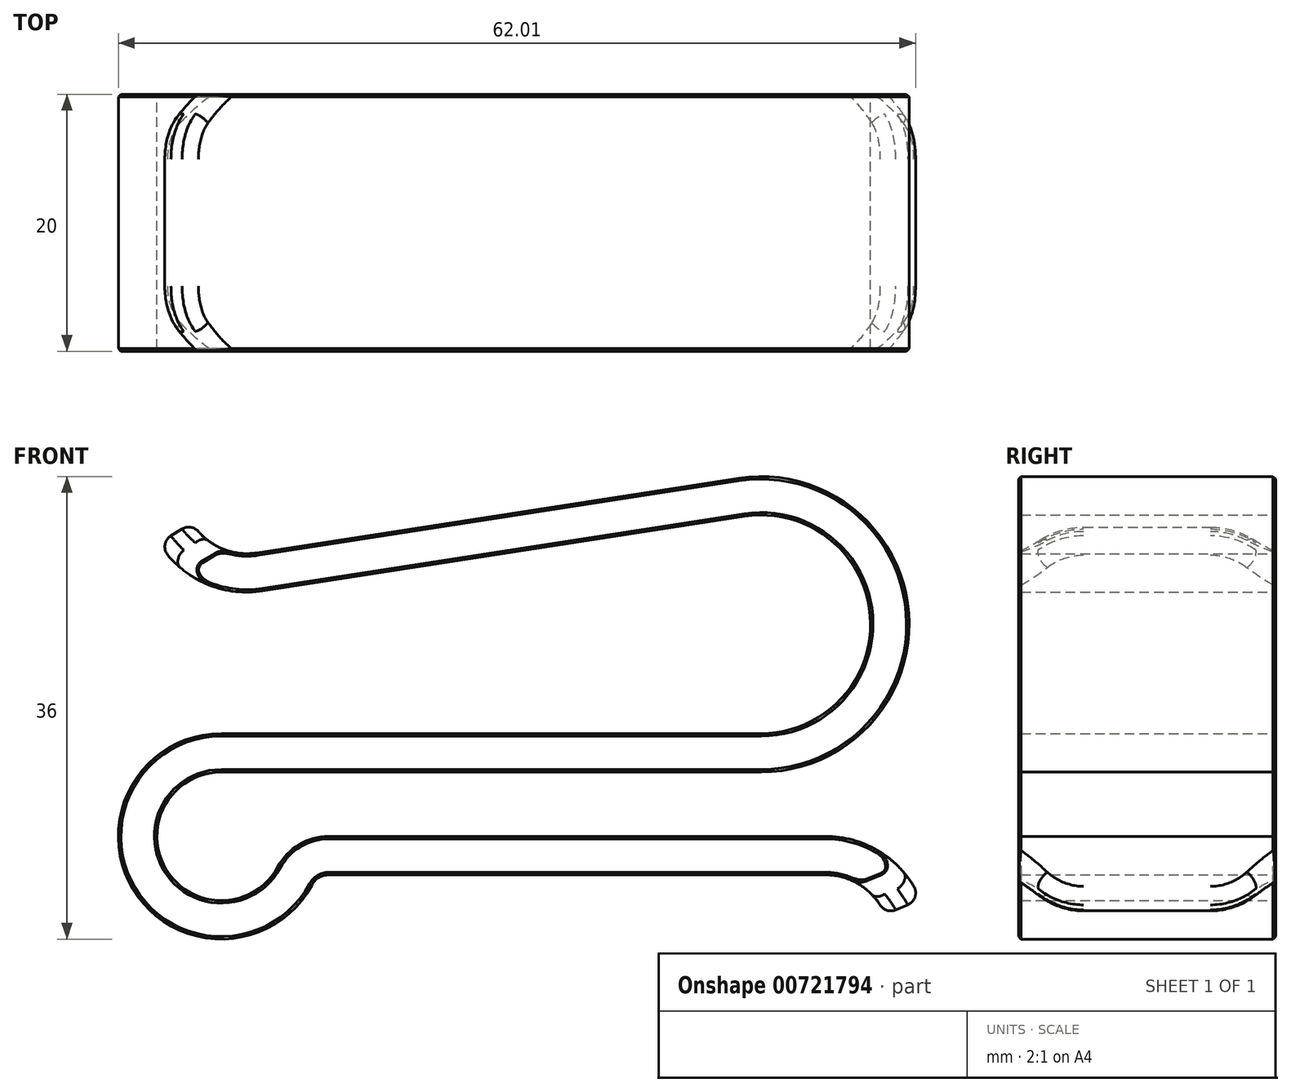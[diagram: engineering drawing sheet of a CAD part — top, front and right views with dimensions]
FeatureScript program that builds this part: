
annotation { "Feature Type Name" : "Feature", "Feature Type Description" : "" }
export const myFeature = defineFeature(function(context is Context, id is Id, definition is map)
    precondition{}
    {
        {
            var Q0;
            Q0=qCreatedBy(makeId("Front.planeOp"),FACE);
            var sketch = newSketch(context, id + "F0", { "sketchPlane" : qUnion([Q0])});
            skLineSegment(sketch, "E0", {"start": v(-42, 0) * mm, "end": v(0, 0) * mm, "construction": true});
            skArc(sketch, "E1", {"start": v(0, 0) * mm, "mid": v(9.97, 10.77) * mm, "end": v(-1.53, 19.88) * mm, "construction": true});
            skLineSegment(sketch, "E2", {"start": v(-1.53, 19.88) * mm, "end": v(-39, 14.08) * mm, "construction": true});
            skArc(sketch, "E3", {"start": v(-45.55, 17.11) * mm, "mid": v(-42.74, 14.6) * mm, "end": v(-39, 14.08) * mm, "construction": true});
            skArc(sketch, "E4", {"start": v(-42, 0) * mm, "mid": v(-47.58, -9.83) * mm, "end": v(-36.28, -9.58) * mm, "construction": true});
            skArc(sketch, "E5", {"start": v(-33.63, -8) * mm, "mid": v(-35.17, -8.42) * mm, "end": v(-36.28, -9.58) * mm, "construction": true});
            skLineSegment(sketch, "E6", {"start": v(-33.63, -8) * mm, "end": v(5, -8) * mm, "construction": true});
            skArc(sketch, "E7", {"start": v(11, -12) * mm, "mid": v(8.6, -9.1) * mm, "end": v(5, -8) * mm, "construction": true});
            skArc(sketch, "E8.0", {"start": v(-44.27, 17.9) * mm, "mid": v(-42.1, 15.96) * mm, "end": v(-39.23, 15.56) * mm});
            skLineSegment(sketch, "E8.1", {"start": v(-1.76, 21.36) * mm, "end": v(-39.23, 15.56) * mm});
            skArc(sketch, "E8.2", {"start": v(0, -1.5) * mm, "mid": v(11.47, 10.88) * mm, "end": v(-1.76, 21.36) * mm});
            skLineSegment(sketch, "E8.3", {"start": v(-42, -1.5) * mm, "end": v(0, -1.5) * mm});
            skArc(sketch, "E8.4", {"start": v(12.38, -11.42) * mm, "mid": v(9.44, -7.84) * mm, "end": v(5, -6.5) * mm});
            skLineSegment(sketch, "E8.5", {"start": v(-33.63, -6.5) * mm, "end": v(5, -6.5) * mm});
            skArc(sketch, "E8.6", {"start": v(-33.63, -6.5) * mm, "mid": v(-35.94, -7.14) * mm, "end": v(-37.6, -8.87) * mm});
            skArc(sketch, "E8.7", {"start": v(-42, -1.5) * mm, "mid": v(-46.3, -9.06) * mm, "end": v(-37.6, -8.87) * mm});
            skArc(sketch, "E9.0", {"start": v(9.62, -12.58) * mm, "mid": v(7.77, -10.34) * mm, "end": v(5, -9.5) * mm});
            skLineSegment(sketch, "E9.1", {"start": v(-33.63, -9.5) * mm, "end": v(5, -9.5) * mm});
            skArc(sketch, "E9.2", {"start": v(-33.63, -9.5) * mm, "mid": v(-34.4, -9.71) * mm, "end": v(-34.95, -10.29) * mm});
            skArc(sketch, "E9.3", {"start": v(-42, 1.5) * mm, "mid": v(-48.87, -10.6) * mm, "end": v(-34.95, -10.29) * mm});
            skArc(sketch, "E9.4", {"start": v(-46.83, 16.33) * mm, "mid": v(-43.37, 13.24) * mm, "end": v(-38.78, 12.6) * mm});
            skLineSegment(sketch, "E9.5", {"start": v(-1.3, 18.4) * mm, "end": v(-38.78, 12.6) * mm});
            skArc(sketch, "E9.6", {"start": v(0, 1.5) * mm, "mid": v(8.47, 10.65) * mm, "end": v(-1.3, 18.4) * mm});
            skLineSegment(sketch, "E9.7", {"start": v(-42, 1.5) * mm, "end": v(0, 1.5) * mm});
            skLineSegment(sketch, "E10", {"start": v(12.38, -11.42) * mm, "end": v(9.62, -12.58) * mm});
            skLineSegment(sketch, "E11", {"start": v(-44.27, 17.9) * mm, "end": v(-46.83, 16.33) * mm});
            skSolve(sketch);
        }
        {
            var Q0;
            Q0=makeQuery(id+"F0.imprint","IMPRINT",FACE,{"disambiguationData":[TD([[makeQuery(id+"F0.imprint","IMPRINT",EDGE,{"derivedFrom":sQuery(id+"F0.wireOp",EDGE,"E8.0")}),-1.0]])]});
            extrude(context, id + "F1", {"entities" : qUnion([Q0]), "depth" : 20 * mm, "offsetDistance" : 25 * mm});
        }
        {
            var Q0;
            Q0=makeQuery(id+"F1.opExtrude","CAP_EDGE",EDGE,{"disambiguationData":[OSD([sQuery(id+"F0.wireOp",EDGE,"E10")])],"isStart":false});
            var Q1;
            Q1=makeQuery(id+"F1.opExtrude","CAP_EDGE",EDGE,{"disambiguationData":[OSD([sQuery(id+"F0.wireOp",EDGE,"E10")])],"isStart":true});
            var Q2;
            Q2=makeQuery(id+"F1.opExtrude","CAP_EDGE",EDGE,{"disambiguationData":[OSD([sQuery(id+"F0.wireOp",EDGE,"E11")])],"isStart":false});
            var Q3;
            Q3=makeQuery(id+"F1.opExtrude","CAP_EDGE",EDGE,{"disambiguationData":[OSD([sQuery(id+"F0.wireOp",EDGE,"E11")])],"isStart":true});
            chamfer(context, id + "F2", {"entities" : qUnion([Q0, Q1, Q2, Q3]), "width" : 3 * mm, "tangentPropagation" : true});
        }
        {
            var Q0;
            {var subQ0=sQuery(id+"F0.wireOp",EDGE,"E11");Q0=makeQuery(id+"F2.opChamfer","BLEND_EDGE",EDGE,{"blendedFrom":[makeQuery(id+"F1.opExtrude","CAP_EDGE",EDGE,{"disambiguationData":[OSD([subQ0])],"isStart":false}),makeQuery(id+"F1.opExtrude","SWEPT_FACE",FACE,{"disambiguationData":[OSD([subQ0])]})],"blendedInto":[makeQuery(id+"F1.opExtrude","SWEPT_FACE",FACE,{"disambiguationData":[OSD([subQ0])]})]});}
            var Q1;
            {var subQ0=sQuery(id+"F0.wireOp",EDGE,"E11");Q1=makeQuery(id+"F2.opChamfer","BLEND_EDGE",EDGE,{"blendedFrom":[makeQuery(id+"F1.opExtrude","CAP_EDGE",EDGE,{"disambiguationData":[OSD([subQ0])],"isStart":true}),makeQuery(id+"F1.opExtrude","SWEPT_FACE",FACE,{"disambiguationData":[OSD([subQ0])]})],"blendedInto":[makeQuery(id+"F1.opExtrude","SWEPT_FACE",FACE,{"disambiguationData":[OSD([subQ0])]})]});}
            var Q2;
            {var subQ0=sQuery(id+"F0.wireOp",EDGE,"E10");Q2=makeQuery(id+"F2.opChamfer","BLEND_EDGE",EDGE,{"blendedFrom":[makeQuery(id+"F1.opExtrude","CAP_EDGE",EDGE,{"disambiguationData":[OSD([subQ0])],"isStart":true}),makeQuery(id+"F1.opExtrude","SWEPT_FACE",FACE,{"disambiguationData":[OSD([subQ0])]})],"blendedInto":[makeQuery(id+"F1.opExtrude","SWEPT_FACE",FACE,{"disambiguationData":[OSD([subQ0])]})]});}
            var Q3;
            {var subQ0=sQuery(id+"F0.wireOp",EDGE,"E10");Q3=makeQuery(id+"F2.opChamfer","BLEND_EDGE",EDGE,{"blendedFrom":[makeQuery(id+"F1.opExtrude","CAP_EDGE",EDGE,{"disambiguationData":[OSD([subQ0])],"isStart":false}),makeQuery(id+"F1.opExtrude","SWEPT_FACE",FACE,{"disambiguationData":[OSD([subQ0])]})],"blendedInto":[makeQuery(id+"F1.opExtrude","SWEPT_FACE",FACE,{"disambiguationData":[OSD([subQ0])]})]});}
            fillet(context, id + "F3", {"entities" : qUnion([Q0, Q1, Q2, Q3]), "radius" : 5 * mm, "tangentPropagation" : true, "allowEdgeOverflow" : false});
        }
        {
            var Q0;
            Q0=makeQuery(id+"F2.opChamfer","BLEND_EDGE",EDGE,{"blendedFrom":[makeQuery(id+"F1.opExtrude","CAP_EDGE",EDGE,{"disambiguationData":[OSD([sQuery(id+"F0.wireOp",EDGE,"E10")])],"isStart":true}),makeQuery(id+"F1.opExtrude","SWEPT_FACE",FACE,{"disambiguationData":[OSD([sQuery(id+"F0.wireOp",EDGE,"E9.0")])]})],"blendedInto":[makeQuery(id+"F1.opExtrude","SWEPT_FACE",FACE,{"disambiguationData":[OSD([sQuery(id+"F0.wireOp",EDGE,"E9.0")])]})]});
            var Q1;
            {var subQ0=sQuery(id+"F0.wireOp",EDGE,"E10");Q1=makeQuery(id+"F3.opFillet","BLEND_EDGE",EDGE,{"blendedFrom":[makeQuery(id+"F2.opChamfer","BLEND_EDGE",EDGE,{"blendedFrom":[makeQuery(id+"F1.opExtrude","CAP_EDGE",EDGE,{"disambiguationData":[OSD([subQ0])],"isStart":true}),makeQuery(id+"F1.opExtrude","SWEPT_FACE",FACE,{"disambiguationData":[OSD([subQ0])]})],"blendedInto":[makeQuery(id+"F1.opExtrude","SWEPT_FACE",FACE,{"disambiguationData":[OSD([subQ0])]})]}),makeQuery(id+"F1.opExtrude","SWEPT_FACE",FACE,{"disambiguationData":[OSD([sQuery(id+"F0.wireOp",EDGE,"E9.0")])]})],"blendedInto":[makeQuery(id+"F1.opExtrude","SWEPT_FACE",FACE,{"disambiguationData":[OSD([sQuery(id+"F0.wireOp",EDGE,"E9.0")])]})]});}
            var Q2;
            Q2=makeQuery(id+"F1.opExtrude","SWEPT_EDGE",EDGE,{"disambiguationData":[OSD([sQuery(id+"F0.wireOp",EDGE,"E9.0"),sQuery(id+"F0.wireOp",EDGE,"E10")])]});
            var Q3;
            {var subQ0=sQuery(id+"F0.wireOp",EDGE,"E10");Q3=makeQuery(id+"F3.opFillet","BLEND_EDGE",EDGE,{"blendedFrom":[makeQuery(id+"F2.opChamfer","BLEND_EDGE",EDGE,{"blendedFrom":[makeQuery(id+"F1.opExtrude","CAP_EDGE",EDGE,{"disambiguationData":[OSD([subQ0])],"isStart":false}),makeQuery(id+"F1.opExtrude","SWEPT_FACE",FACE,{"disambiguationData":[OSD([subQ0])]})],"blendedInto":[makeQuery(id+"F1.opExtrude","SWEPT_FACE",FACE,{"disambiguationData":[OSD([subQ0])]})]}),makeQuery(id+"F1.opExtrude","SWEPT_FACE",FACE,{"disambiguationData":[OSD([sQuery(id+"F0.wireOp",EDGE,"E9.0")])]})],"blendedInto":[makeQuery(id+"F1.opExtrude","SWEPT_FACE",FACE,{"disambiguationData":[OSD([sQuery(id+"F0.wireOp",EDGE,"E9.0")])]})]});}
            var Q4;
            Q4=makeQuery(id+"F2.opChamfer","BLEND_EDGE",EDGE,{"blendedFrom":[makeQuery(id+"F1.opExtrude","CAP_EDGE",EDGE,{"disambiguationData":[OSD([sQuery(id+"F0.wireOp",EDGE,"E10")])],"isStart":false}),makeQuery(id+"F1.opExtrude","SWEPT_FACE",FACE,{"disambiguationData":[OSD([sQuery(id+"F0.wireOp",EDGE,"E9.0")])]})],"blendedInto":[makeQuery(id+"F1.opExtrude","SWEPT_FACE",FACE,{"disambiguationData":[OSD([sQuery(id+"F0.wireOp",EDGE,"E9.0")])]})]});
            var Q5;
            Q5=makeQuery(id+"F1.opExtrude","SWEPT_EDGE",EDGE,{"disambiguationData":[OSD([sQuery(id+"F0.wireOp",EDGE,"E8.4"),sQuery(id+"F0.wireOp",EDGE,"E10")])]});
            var Q6;
            {var subQ0=sQuery(id+"F0.wireOp",EDGE,"E10");Q6=makeQuery(id+"F3.opFillet","BLEND_EDGE",EDGE,{"blendedFrom":[makeQuery(id+"F2.opChamfer","BLEND_EDGE",EDGE,{"blendedFrom":[makeQuery(id+"F1.opExtrude","CAP_EDGE",EDGE,{"disambiguationData":[OSD([subQ0])],"isStart":true}),makeQuery(id+"F1.opExtrude","SWEPT_FACE",FACE,{"disambiguationData":[OSD([subQ0])]})],"blendedInto":[makeQuery(id+"F1.opExtrude","SWEPT_FACE",FACE,{"disambiguationData":[OSD([subQ0])]})]}),makeQuery(id+"F1.opExtrude","SWEPT_FACE",FACE,{"disambiguationData":[OSD([sQuery(id+"F0.wireOp",EDGE,"E8.4")])]})],"blendedInto":[makeQuery(id+"F1.opExtrude","SWEPT_FACE",FACE,{"disambiguationData":[OSD([sQuery(id+"F0.wireOp",EDGE,"E8.4")])]})]});}
            var Q7;
            Q7=makeQuery(id+"F2.opChamfer","BLEND_EDGE",EDGE,{"blendedFrom":[makeQuery(id+"F1.opExtrude","CAP_EDGE",EDGE,{"disambiguationData":[OSD([sQuery(id+"F0.wireOp",EDGE,"E10")])],"isStart":true}),makeQuery(id+"F1.opExtrude","SWEPT_FACE",FACE,{"disambiguationData":[OSD([sQuery(id+"F0.wireOp",EDGE,"E8.4")])]})],"blendedInto":[makeQuery(id+"F1.opExtrude","SWEPT_FACE",FACE,{"disambiguationData":[OSD([sQuery(id+"F0.wireOp",EDGE,"E8.4")])]})]});
            var Q8;
            {var subQ0=sQuery(id+"F0.wireOp",EDGE,"E10");Q8=makeQuery(id+"F3.opFillet","BLEND_EDGE",EDGE,{"blendedFrom":[makeQuery(id+"F2.opChamfer","BLEND_EDGE",EDGE,{"blendedFrom":[makeQuery(id+"F1.opExtrude","CAP_EDGE",EDGE,{"disambiguationData":[OSD([subQ0])],"isStart":false}),makeQuery(id+"F1.opExtrude","SWEPT_FACE",FACE,{"disambiguationData":[OSD([subQ0])]})],"blendedInto":[makeQuery(id+"F1.opExtrude","SWEPT_FACE",FACE,{"disambiguationData":[OSD([subQ0])]})]}),makeQuery(id+"F1.opExtrude","SWEPT_FACE",FACE,{"disambiguationData":[OSD([sQuery(id+"F0.wireOp",EDGE,"E8.4")])]})],"blendedInto":[makeQuery(id+"F1.opExtrude","SWEPT_FACE",FACE,{"disambiguationData":[OSD([sQuery(id+"F0.wireOp",EDGE,"E8.4")])]})]});}
            var Q9;
            Q9=makeQuery(id+"F2.opChamfer","BLEND_EDGE",EDGE,{"blendedFrom":[makeQuery(id+"F1.opExtrude","CAP_EDGE",EDGE,{"disambiguationData":[OSD([sQuery(id+"F0.wireOp",EDGE,"E10")])],"isStart":false}),makeQuery(id+"F1.opExtrude","SWEPT_FACE",FACE,{"disambiguationData":[OSD([sQuery(id+"F0.wireOp",EDGE,"E8.4")])]})],"blendedInto":[makeQuery(id+"F1.opExtrude","SWEPT_FACE",FACE,{"disambiguationData":[OSD([sQuery(id+"F0.wireOp",EDGE,"E8.4")])]})]});
            var Q10;
            Q10=makeQuery(id+"F2.opChamfer","BLEND_EDGE",EDGE,{"blendedFrom":[makeQuery(id+"F1.opExtrude","CAP_EDGE",EDGE,{"disambiguationData":[OSD([sQuery(id+"F0.wireOp",EDGE,"E11")])],"isStart":false}),makeQuery(id+"F1.opExtrude","SWEPT_FACE",FACE,{"disambiguationData":[OSD([sQuery(id+"F0.wireOp",EDGE,"E8.0")])]})],"blendedInto":[makeQuery(id+"F1.opExtrude","SWEPT_FACE",FACE,{"disambiguationData":[OSD([sQuery(id+"F0.wireOp",EDGE,"E8.0")])]})]});
            var Q11;
            {var subQ0=sQuery(id+"F0.wireOp",EDGE,"E11");Q11=makeQuery(id+"F3.opFillet","BLEND_EDGE",EDGE,{"blendedFrom":[makeQuery(id+"F2.opChamfer","BLEND_EDGE",EDGE,{"blendedFrom":[makeQuery(id+"F1.opExtrude","CAP_EDGE",EDGE,{"disambiguationData":[OSD([subQ0])],"isStart":false}),makeQuery(id+"F1.opExtrude","SWEPT_FACE",FACE,{"disambiguationData":[OSD([subQ0])]})],"blendedInto":[makeQuery(id+"F1.opExtrude","SWEPT_FACE",FACE,{"disambiguationData":[OSD([subQ0])]})]}),makeQuery(id+"F1.opExtrude","SWEPT_FACE",FACE,{"disambiguationData":[OSD([sQuery(id+"F0.wireOp",EDGE,"E8.0")])]})],"blendedInto":[makeQuery(id+"F1.opExtrude","SWEPT_FACE",FACE,{"disambiguationData":[OSD([sQuery(id+"F0.wireOp",EDGE,"E8.0")])]})]});}
            var Q12;
            Q12=makeQuery(id+"F1.opExtrude","SWEPT_EDGE",EDGE,{"disambiguationData":[OSD([sQuery(id+"F0.wireOp",EDGE,"E8.0"),sQuery(id+"F0.wireOp",EDGE,"E11")])]});
            var Q13;
            {var subQ0=sQuery(id+"F0.wireOp",EDGE,"E11");Q13=makeQuery(id+"F3.opFillet","BLEND_EDGE",EDGE,{"blendedFrom":[makeQuery(id+"F2.opChamfer","BLEND_EDGE",EDGE,{"blendedFrom":[makeQuery(id+"F1.opExtrude","CAP_EDGE",EDGE,{"disambiguationData":[OSD([subQ0])],"isStart":true}),makeQuery(id+"F1.opExtrude","SWEPT_FACE",FACE,{"disambiguationData":[OSD([subQ0])]})],"blendedInto":[makeQuery(id+"F1.opExtrude","SWEPT_FACE",FACE,{"disambiguationData":[OSD([subQ0])]})]}),makeQuery(id+"F1.opExtrude","SWEPT_FACE",FACE,{"disambiguationData":[OSD([sQuery(id+"F0.wireOp",EDGE,"E8.0")])]})],"blendedInto":[makeQuery(id+"F1.opExtrude","SWEPT_FACE",FACE,{"disambiguationData":[OSD([sQuery(id+"F0.wireOp",EDGE,"E8.0")])]})]});}
            var Q14;
            Q14=makeQuery(id+"F2.opChamfer","BLEND_EDGE",EDGE,{"blendedFrom":[makeQuery(id+"F1.opExtrude","CAP_EDGE",EDGE,{"disambiguationData":[OSD([sQuery(id+"F0.wireOp",EDGE,"E11")])],"isStart":true}),makeQuery(id+"F1.opExtrude","SWEPT_FACE",FACE,{"disambiguationData":[OSD([sQuery(id+"F0.wireOp",EDGE,"E8.0")])]})],"blendedInto":[makeQuery(id+"F1.opExtrude","SWEPT_FACE",FACE,{"disambiguationData":[OSD([sQuery(id+"F0.wireOp",EDGE,"E8.0")])]})]});
            var Q15;
            Q15=makeQuery(id+"F2.opChamfer","BLEND_EDGE",EDGE,{"blendedFrom":[makeQuery(id+"F1.opExtrude","CAP_EDGE",EDGE,{"disambiguationData":[OSD([sQuery(id+"F0.wireOp",EDGE,"E11")])],"isStart":false}),makeQuery(id+"F1.opExtrude","SWEPT_FACE",FACE,{"disambiguationData":[OSD([sQuery(id+"F0.wireOp",EDGE,"E9.4")])]})],"blendedInto":[makeQuery(id+"F1.opExtrude","SWEPT_FACE",FACE,{"disambiguationData":[OSD([sQuery(id+"F0.wireOp",EDGE,"E9.4")])]})]});
            var Q16;
            {var subQ0=sQuery(id+"F0.wireOp",EDGE,"E11");Q16=makeQuery(id+"F3.opFillet","BLEND_EDGE",EDGE,{"blendedFrom":[makeQuery(id+"F2.opChamfer","BLEND_EDGE",EDGE,{"blendedFrom":[makeQuery(id+"F1.opExtrude","CAP_EDGE",EDGE,{"disambiguationData":[OSD([subQ0])],"isStart":false}),makeQuery(id+"F1.opExtrude","SWEPT_FACE",FACE,{"disambiguationData":[OSD([subQ0])]})],"blendedInto":[makeQuery(id+"F1.opExtrude","SWEPT_FACE",FACE,{"disambiguationData":[OSD([subQ0])]})]}),makeQuery(id+"F1.opExtrude","SWEPT_FACE",FACE,{"disambiguationData":[OSD([sQuery(id+"F0.wireOp",EDGE,"E9.4")])]})],"blendedInto":[makeQuery(id+"F1.opExtrude","SWEPT_FACE",FACE,{"disambiguationData":[OSD([sQuery(id+"F0.wireOp",EDGE,"E9.4")])]})]});}
            var Q17;
            Q17=makeQuery(id+"F1.opExtrude","SWEPT_EDGE",EDGE,{"disambiguationData":[OSD([sQuery(id+"F0.wireOp",EDGE,"E9.4"),sQuery(id+"F0.wireOp",EDGE,"E11")])]});
            var Q18;
            {var subQ0=sQuery(id+"F0.wireOp",EDGE,"E11");Q18=makeQuery(id+"F3.opFillet","BLEND_EDGE",EDGE,{"blendedFrom":[makeQuery(id+"F2.opChamfer","BLEND_EDGE",EDGE,{"blendedFrom":[makeQuery(id+"F1.opExtrude","CAP_EDGE",EDGE,{"disambiguationData":[OSD([subQ0])],"isStart":true}),makeQuery(id+"F1.opExtrude","SWEPT_FACE",FACE,{"disambiguationData":[OSD([subQ0])]})],"blendedInto":[makeQuery(id+"F1.opExtrude","SWEPT_FACE",FACE,{"disambiguationData":[OSD([subQ0])]})]}),makeQuery(id+"F1.opExtrude","SWEPT_FACE",FACE,{"disambiguationData":[OSD([sQuery(id+"F0.wireOp",EDGE,"E9.4")])]})],"blendedInto":[makeQuery(id+"F1.opExtrude","SWEPT_FACE",FACE,{"disambiguationData":[OSD([sQuery(id+"F0.wireOp",EDGE,"E9.4")])]})]});}
            var Q19;
            Q19=makeQuery(id+"F2.opChamfer","BLEND_EDGE",EDGE,{"blendedFrom":[makeQuery(id+"F1.opExtrude","CAP_EDGE",EDGE,{"disambiguationData":[OSD([sQuery(id+"F0.wireOp",EDGE,"E11")])],"isStart":true}),makeQuery(id+"F1.opExtrude","SWEPT_FACE",FACE,{"disambiguationData":[OSD([sQuery(id+"F0.wireOp",EDGE,"E9.4")])]})],"blendedInto":[makeQuery(id+"F1.opExtrude","SWEPT_FACE",FACE,{"disambiguationData":[OSD([sQuery(id+"F0.wireOp",EDGE,"E9.4")])]})]});
            fillet(context, id + "F4", {"entities" : qUnion([Q0, Q1, Q2, Q3, Q4, Q5, Q6, Q7, Q8, Q9, Q10, Q11, Q12, Q13, Q14, Q15, Q16, Q17, Q18, Q19]), "radius" : 1 * mm, "tangentPropagation" : true, "allowEdgeOverflow" : false});
        }
        {
            var Q0;
            Q0=makeQuery(id+"F1.opExtrude","CAP_EDGE",EDGE,{"disambiguationData":[OSD([sQuery(id+"F0.wireOp",EDGE,"E8.1")])],"isStart":true});
            var Q1;
            Q1=makeQuery(id+"F1.opExtrude","CAP_EDGE",EDGE,{"disambiguationData":[OSD([sQuery(id+"F0.wireOp",EDGE,"E8.2")])],"isStart":true});
            var Q2;
            Q2=makeQuery(id+"F1.opExtrude","CAP_EDGE",EDGE,{"disambiguationData":[OSD([sQuery(id+"F0.wireOp",EDGE,"E8.3")])],"isStart":true});
            var Q3;
            Q3=makeQuery(id+"F1.opExtrude","CAP_EDGE",EDGE,{"disambiguationData":[OSD([sQuery(id+"F0.wireOp",EDGE,"E8.7")])],"isStart":true});
            var Q4;
            Q4=makeQuery(id+"F1.opExtrude","CAP_EDGE",EDGE,{"disambiguationData":[OSD([sQuery(id+"F0.wireOp",EDGE,"E8.6")])],"isStart":true});
            var Q5;
            Q5=makeQuery(id+"F1.opExtrude","CAP_EDGE",EDGE,{"disambiguationData":[OSD([sQuery(id+"F0.wireOp",EDGE,"E8.5")])],"isStart":true});
            var Q6;
            Q6=makeQuery(id+"F1.opExtrude","CAP_EDGE",EDGE,{"disambiguationData":[OSD([sQuery(id+"F0.wireOp",EDGE,"E8.4")])],"isStart":true});
            var Q7;
            {var subQ0=sQuery(id+"F0.wireOp",EDGE,"E10");var subQ1=sQuery(id+"F0.wireOp",EDGE,"E8.4");Q7=makeQuery(id+"F4.opFillet","BLEND_EDGE",EDGE,{"blendedFrom":[makeQuery(id+"F2.opChamfer","BLEND_EDGE",EDGE,{"blendedFrom":[makeQuery(id+"F1.opExtrude","CAP_EDGE",EDGE,{"disambiguationData":[OSD([subQ0])],"isStart":true}),makeQuery(id+"F1.opExtrude","SWEPT_FACE",FACE,{"disambiguationData":[OSD([subQ1])]})],"blendedInto":[makeQuery(id+"F1.opExtrude","SWEPT_FACE",FACE,{"disambiguationData":[OSD([subQ1])]})]}),makeQuery(id+"F1.opExtrude","CAP_FACE",FACE,{"disambiguationData":[OSD([sQuery(id+"F0.wireOp",EDGE,"E8.0"),sQuery(id+"F0.wireOp",EDGE,"E8.1"),sQuery(id+"F0.wireOp",EDGE,"E8.2"),sQuery(id+"F0.wireOp",EDGE,"E8.3"),subQ1,sQuery(id+"F0.wireOp",EDGE,"E8.5"),sQuery(id+"F0.wireOp",EDGE,"E8.6"),sQuery(id+"F0.wireOp",EDGE,"E8.7"),sQuery(id+"F0.wireOp",EDGE,"E9.0"),sQuery(id+"F0.wireOp",EDGE,"E9.1"),sQuery(id+"F0.wireOp",EDGE,"E9.2"),sQuery(id+"F0.wireOp",EDGE,"E9.3"),sQuery(id+"F0.wireOp",EDGE,"E9.4"),sQuery(id+"F0.wireOp",EDGE,"E9.5"),sQuery(id+"F0.wireOp",EDGE,"E9.6"),sQuery(id+"F0.wireOp",EDGE,"E9.7"),subQ0,sQuery(id+"F0.wireOp",EDGE,"E11")])],"isStart":true})],"blendedInto":[makeQuery(id+"F1.opExtrude","CAP_FACE",FACE,{"disambiguationData":[OSD([sQuery(id+"F0.wireOp",EDGE,"E8.0"),sQuery(id+"F0.wireOp",EDGE,"E8.1"),sQuery(id+"F0.wireOp",EDGE,"E8.2"),sQuery(id+"F0.wireOp",EDGE,"E8.3"),subQ1,sQuery(id+"F0.wireOp",EDGE,"E8.5"),sQuery(id+"F0.wireOp",EDGE,"E8.6"),sQuery(id+"F0.wireOp",EDGE,"E8.7"),sQuery(id+"F0.wireOp",EDGE,"E9.0"),sQuery(id+"F0.wireOp",EDGE,"E9.1"),sQuery(id+"F0.wireOp",EDGE,"E9.2"),sQuery(id+"F0.wireOp",EDGE,"E9.3"),sQuery(id+"F0.wireOp",EDGE,"E9.4"),sQuery(id+"F0.wireOp",EDGE,"E9.5"),sQuery(id+"F0.wireOp",EDGE,"E9.6"),sQuery(id+"F0.wireOp",EDGE,"E9.7"),subQ0,sQuery(id+"F0.wireOp",EDGE,"E11")])],"isStart":true})]});}
            var Q8;
            {var subQ0=sQuery(id+"F0.wireOp",EDGE,"E10");Q8=makeQuery(id+"F2.opChamfer","BLEND_EDGE",EDGE,{"blendedFrom":[makeQuery(id+"F1.opExtrude","CAP_EDGE",EDGE,{"disambiguationData":[OSD([subQ0])],"isStart":true}),makeQuery(id+"F1.opExtrude","CAP_FACE",FACE,{"disambiguationData":[OSD([sQuery(id+"F0.wireOp",EDGE,"E8.0"),sQuery(id+"F0.wireOp",EDGE,"E8.1"),sQuery(id+"F0.wireOp",EDGE,"E8.2"),sQuery(id+"F0.wireOp",EDGE,"E8.3"),sQuery(id+"F0.wireOp",EDGE,"E8.4"),sQuery(id+"F0.wireOp",EDGE,"E8.5"),sQuery(id+"F0.wireOp",EDGE,"E8.6"),sQuery(id+"F0.wireOp",EDGE,"E8.7"),sQuery(id+"F0.wireOp",EDGE,"E9.0"),sQuery(id+"F0.wireOp",EDGE,"E9.1"),sQuery(id+"F0.wireOp",EDGE,"E9.2"),sQuery(id+"F0.wireOp",EDGE,"E9.3"),sQuery(id+"F0.wireOp",EDGE,"E9.4"),sQuery(id+"F0.wireOp",EDGE,"E9.5"),sQuery(id+"F0.wireOp",EDGE,"E9.6"),sQuery(id+"F0.wireOp",EDGE,"E9.7"),subQ0,sQuery(id+"F0.wireOp",EDGE,"E11")])],"isStart":true})],"blendedInto":[makeQuery(id+"F1.opExtrude","CAP_FACE",FACE,{"disambiguationData":[OSD([sQuery(id+"F0.wireOp",EDGE,"E8.0"),sQuery(id+"F0.wireOp",EDGE,"E8.1"),sQuery(id+"F0.wireOp",EDGE,"E8.2"),sQuery(id+"F0.wireOp",EDGE,"E8.3"),sQuery(id+"F0.wireOp",EDGE,"E8.4"),sQuery(id+"F0.wireOp",EDGE,"E8.5"),sQuery(id+"F0.wireOp",EDGE,"E8.6"),sQuery(id+"F0.wireOp",EDGE,"E8.7"),sQuery(id+"F0.wireOp",EDGE,"E9.0"),sQuery(id+"F0.wireOp",EDGE,"E9.1"),sQuery(id+"F0.wireOp",EDGE,"E9.2"),sQuery(id+"F0.wireOp",EDGE,"E9.3"),sQuery(id+"F0.wireOp",EDGE,"E9.4"),sQuery(id+"F0.wireOp",EDGE,"E9.5"),sQuery(id+"F0.wireOp",EDGE,"E9.6"),sQuery(id+"F0.wireOp",EDGE,"E9.7"),subQ0,sQuery(id+"F0.wireOp",EDGE,"E11")])],"isStart":true})]});}
            var Q9;
            {var subQ0=sQuery(id+"F0.wireOp",EDGE,"E10");var subQ1=sQuery(id+"F0.wireOp",EDGE,"E9.0");Q9=makeQuery(id+"F4.opFillet","BLEND_EDGE",EDGE,{"blendedFrom":[makeQuery(id+"F2.opChamfer","BLEND_EDGE",EDGE,{"blendedFrom":[makeQuery(id+"F1.opExtrude","CAP_EDGE",EDGE,{"disambiguationData":[OSD([subQ0])],"isStart":true}),makeQuery(id+"F1.opExtrude","SWEPT_FACE",FACE,{"disambiguationData":[OSD([subQ1])]})],"blendedInto":[makeQuery(id+"F1.opExtrude","SWEPT_FACE",FACE,{"disambiguationData":[OSD([subQ1])]})]}),makeQuery(id+"F1.opExtrude","CAP_FACE",FACE,{"disambiguationData":[OSD([sQuery(id+"F0.wireOp",EDGE,"E8.0"),sQuery(id+"F0.wireOp",EDGE,"E8.1"),sQuery(id+"F0.wireOp",EDGE,"E8.2"),sQuery(id+"F0.wireOp",EDGE,"E8.3"),sQuery(id+"F0.wireOp",EDGE,"E8.4"),sQuery(id+"F0.wireOp",EDGE,"E8.5"),sQuery(id+"F0.wireOp",EDGE,"E8.6"),sQuery(id+"F0.wireOp",EDGE,"E8.7"),subQ1,sQuery(id+"F0.wireOp",EDGE,"E9.1"),sQuery(id+"F0.wireOp",EDGE,"E9.2"),sQuery(id+"F0.wireOp",EDGE,"E9.3"),sQuery(id+"F0.wireOp",EDGE,"E9.4"),sQuery(id+"F0.wireOp",EDGE,"E9.5"),sQuery(id+"F0.wireOp",EDGE,"E9.6"),sQuery(id+"F0.wireOp",EDGE,"E9.7"),subQ0,sQuery(id+"F0.wireOp",EDGE,"E11")])],"isStart":true})],"blendedInto":[makeQuery(id+"F1.opExtrude","CAP_FACE",FACE,{"disambiguationData":[OSD([sQuery(id+"F0.wireOp",EDGE,"E8.0"),sQuery(id+"F0.wireOp",EDGE,"E8.1"),sQuery(id+"F0.wireOp",EDGE,"E8.2"),sQuery(id+"F0.wireOp",EDGE,"E8.3"),sQuery(id+"F0.wireOp",EDGE,"E8.4"),sQuery(id+"F0.wireOp",EDGE,"E8.5"),sQuery(id+"F0.wireOp",EDGE,"E8.6"),sQuery(id+"F0.wireOp",EDGE,"E8.7"),subQ1,sQuery(id+"F0.wireOp",EDGE,"E9.1"),sQuery(id+"F0.wireOp",EDGE,"E9.2"),sQuery(id+"F0.wireOp",EDGE,"E9.3"),sQuery(id+"F0.wireOp",EDGE,"E9.4"),sQuery(id+"F0.wireOp",EDGE,"E9.5"),sQuery(id+"F0.wireOp",EDGE,"E9.6"),sQuery(id+"F0.wireOp",EDGE,"E9.7"),subQ0,sQuery(id+"F0.wireOp",EDGE,"E11")])],"isStart":true})]});}
            var Q10;
            Q10=makeQuery(id+"F1.opExtrude","CAP_EDGE",EDGE,{"disambiguationData":[OSD([sQuery(id+"F0.wireOp",EDGE,"E9.0")])],"isStart":true});
            var Q11;
            Q11=makeQuery(id+"F1.opExtrude","CAP_EDGE",EDGE,{"disambiguationData":[OSD([sQuery(id+"F0.wireOp",EDGE,"E9.1")])],"isStart":true});
            var Q12;
            Q12=makeQuery(id+"F1.opExtrude","CAP_EDGE",EDGE,{"disambiguationData":[OSD([sQuery(id+"F0.wireOp",EDGE,"E9.2")])],"isStart":true});
            var Q13;
            Q13=makeQuery(id+"F1.opExtrude","CAP_EDGE",EDGE,{"disambiguationData":[OSD([sQuery(id+"F0.wireOp",EDGE,"E9.3")])],"isStart":true});
            var Q14;
            Q14=makeQuery(id+"F1.opExtrude","CAP_EDGE",EDGE,{"disambiguationData":[OSD([sQuery(id+"F0.wireOp",EDGE,"E9.7")])],"isStart":true});
            var Q15;
            Q15=makeQuery(id+"F1.opExtrude","CAP_EDGE",EDGE,{"disambiguationData":[OSD([sQuery(id+"F0.wireOp",EDGE,"E9.6")])],"isStart":true});
            var Q16;
            Q16=makeQuery(id+"F1.opExtrude","CAP_EDGE",EDGE,{"disambiguationData":[OSD([sQuery(id+"F0.wireOp",EDGE,"E9.5")])],"isStart":true});
            var Q17;
            Q17=makeQuery(id+"F1.opExtrude","CAP_EDGE",EDGE,{"disambiguationData":[OSD([sQuery(id+"F0.wireOp",EDGE,"E9.4")])],"isStart":true});
            var Q18;
            {var subQ0=sQuery(id+"F0.wireOp",EDGE,"E11");var subQ1=sQuery(id+"F0.wireOp",EDGE,"E8.0");Q18=makeQuery(id+"F4.opFillet","BLEND_EDGE",EDGE,{"blendedFrom":[makeQuery(id+"F2.opChamfer","BLEND_EDGE",EDGE,{"blendedFrom":[makeQuery(id+"F1.opExtrude","CAP_EDGE",EDGE,{"disambiguationData":[OSD([subQ0])],"isStart":true}),makeQuery(id+"F1.opExtrude","SWEPT_FACE",FACE,{"disambiguationData":[OSD([subQ1])]})],"blendedInto":[makeQuery(id+"F1.opExtrude","SWEPT_FACE",FACE,{"disambiguationData":[OSD([subQ1])]})]}),makeQuery(id+"F1.opExtrude","CAP_FACE",FACE,{"disambiguationData":[OSD([subQ1,sQuery(id+"F0.wireOp",EDGE,"E8.1"),sQuery(id+"F0.wireOp",EDGE,"E8.2"),sQuery(id+"F0.wireOp",EDGE,"E8.3"),sQuery(id+"F0.wireOp",EDGE,"E8.4"),sQuery(id+"F0.wireOp",EDGE,"E8.5"),sQuery(id+"F0.wireOp",EDGE,"E8.6"),sQuery(id+"F0.wireOp",EDGE,"E8.7"),sQuery(id+"F0.wireOp",EDGE,"E9.0"),sQuery(id+"F0.wireOp",EDGE,"E9.1"),sQuery(id+"F0.wireOp",EDGE,"E9.2"),sQuery(id+"F0.wireOp",EDGE,"E9.3"),sQuery(id+"F0.wireOp",EDGE,"E9.4"),sQuery(id+"F0.wireOp",EDGE,"E9.5"),sQuery(id+"F0.wireOp",EDGE,"E9.6"),sQuery(id+"F0.wireOp",EDGE,"E9.7"),sQuery(id+"F0.wireOp",EDGE,"E10"),subQ0])],"isStart":true})],"blendedInto":[makeQuery(id+"F1.opExtrude","CAP_FACE",FACE,{"disambiguationData":[OSD([subQ1,sQuery(id+"F0.wireOp",EDGE,"E8.1"),sQuery(id+"F0.wireOp",EDGE,"E8.2"),sQuery(id+"F0.wireOp",EDGE,"E8.3"),sQuery(id+"F0.wireOp",EDGE,"E8.4"),sQuery(id+"F0.wireOp",EDGE,"E8.5"),sQuery(id+"F0.wireOp",EDGE,"E8.6"),sQuery(id+"F0.wireOp",EDGE,"E8.7"),sQuery(id+"F0.wireOp",EDGE,"E9.0"),sQuery(id+"F0.wireOp",EDGE,"E9.1"),sQuery(id+"F0.wireOp",EDGE,"E9.2"),sQuery(id+"F0.wireOp",EDGE,"E9.3"),sQuery(id+"F0.wireOp",EDGE,"E9.4"),sQuery(id+"F0.wireOp",EDGE,"E9.5"),sQuery(id+"F0.wireOp",EDGE,"E9.6"),sQuery(id+"F0.wireOp",EDGE,"E9.7"),sQuery(id+"F0.wireOp",EDGE,"E10"),subQ0])],"isStart":true})]});}
            var Q19;
            Q19=makeQuery(id+"F1.opExtrude","CAP_EDGE",EDGE,{"disambiguationData":[OSD([sQuery(id+"F0.wireOp",EDGE,"E8.0")])],"isStart":true});
            var Q20;
            {var subQ0=sQuery(id+"F0.wireOp",EDGE,"E11");Q20=makeQuery(id+"F2.opChamfer","BLEND_EDGE",EDGE,{"blendedFrom":[makeQuery(id+"F1.opExtrude","CAP_EDGE",EDGE,{"disambiguationData":[OSD([subQ0])],"isStart":true}),makeQuery(id+"F1.opExtrude","CAP_FACE",FACE,{"disambiguationData":[OSD([sQuery(id+"F0.wireOp",EDGE,"E8.0"),sQuery(id+"F0.wireOp",EDGE,"E8.1"),sQuery(id+"F0.wireOp",EDGE,"E8.2"),sQuery(id+"F0.wireOp",EDGE,"E8.3"),sQuery(id+"F0.wireOp",EDGE,"E8.4"),sQuery(id+"F0.wireOp",EDGE,"E8.5"),sQuery(id+"F0.wireOp",EDGE,"E8.6"),sQuery(id+"F0.wireOp",EDGE,"E8.7"),sQuery(id+"F0.wireOp",EDGE,"E9.0"),sQuery(id+"F0.wireOp",EDGE,"E9.1"),sQuery(id+"F0.wireOp",EDGE,"E9.2"),sQuery(id+"F0.wireOp",EDGE,"E9.3"),sQuery(id+"F0.wireOp",EDGE,"E9.4"),sQuery(id+"F0.wireOp",EDGE,"E9.5"),sQuery(id+"F0.wireOp",EDGE,"E9.6"),sQuery(id+"F0.wireOp",EDGE,"E9.7"),sQuery(id+"F0.wireOp",EDGE,"E10"),subQ0])],"isStart":true})],"blendedInto":[makeQuery(id+"F1.opExtrude","CAP_FACE",FACE,{"disambiguationData":[OSD([sQuery(id+"F0.wireOp",EDGE,"E8.0"),sQuery(id+"F0.wireOp",EDGE,"E8.1"),sQuery(id+"F0.wireOp",EDGE,"E8.2"),sQuery(id+"F0.wireOp",EDGE,"E8.3"),sQuery(id+"F0.wireOp",EDGE,"E8.4"),sQuery(id+"F0.wireOp",EDGE,"E8.5"),sQuery(id+"F0.wireOp",EDGE,"E8.6"),sQuery(id+"F0.wireOp",EDGE,"E8.7"),sQuery(id+"F0.wireOp",EDGE,"E9.0"),sQuery(id+"F0.wireOp",EDGE,"E9.1"),sQuery(id+"F0.wireOp",EDGE,"E9.2"),sQuery(id+"F0.wireOp",EDGE,"E9.3"),sQuery(id+"F0.wireOp",EDGE,"E9.4"),sQuery(id+"F0.wireOp",EDGE,"E9.5"),sQuery(id+"F0.wireOp",EDGE,"E9.6"),sQuery(id+"F0.wireOp",EDGE,"E9.7"),sQuery(id+"F0.wireOp",EDGE,"E10"),subQ0])],"isStart":true})]});}
            var Q21;
            {var subQ0=sQuery(id+"F0.wireOp",EDGE,"E10");Q21=makeQuery(id+"F2.opChamfer","BLEND_EDGE",EDGE,{"blendedFrom":[makeQuery(id+"F1.opExtrude","CAP_EDGE",EDGE,{"disambiguationData":[OSD([subQ0])],"isStart":false}),makeQuery(id+"F1.opExtrude","CAP_FACE",FACE,{"disambiguationData":[OSD([sQuery(id+"F0.wireOp",EDGE,"E8.0"),sQuery(id+"F0.wireOp",EDGE,"E8.1"),sQuery(id+"F0.wireOp",EDGE,"E8.2"),sQuery(id+"F0.wireOp",EDGE,"E8.3"),sQuery(id+"F0.wireOp",EDGE,"E8.4"),sQuery(id+"F0.wireOp",EDGE,"E8.5"),sQuery(id+"F0.wireOp",EDGE,"E8.6"),sQuery(id+"F0.wireOp",EDGE,"E8.7"),sQuery(id+"F0.wireOp",EDGE,"E9.0"),sQuery(id+"F0.wireOp",EDGE,"E9.1"),sQuery(id+"F0.wireOp",EDGE,"E9.2"),sQuery(id+"F0.wireOp",EDGE,"E9.3"),sQuery(id+"F0.wireOp",EDGE,"E9.4"),sQuery(id+"F0.wireOp",EDGE,"E9.5"),sQuery(id+"F0.wireOp",EDGE,"E9.6"),sQuery(id+"F0.wireOp",EDGE,"E9.7"),subQ0,sQuery(id+"F0.wireOp",EDGE,"E11")])],"isStart":false})],"blendedInto":[makeQuery(id+"F1.opExtrude","CAP_FACE",FACE,{"disambiguationData":[OSD([sQuery(id+"F0.wireOp",EDGE,"E8.0"),sQuery(id+"F0.wireOp",EDGE,"E8.1"),sQuery(id+"F0.wireOp",EDGE,"E8.2"),sQuery(id+"F0.wireOp",EDGE,"E8.3"),sQuery(id+"F0.wireOp",EDGE,"E8.4"),sQuery(id+"F0.wireOp",EDGE,"E8.5"),sQuery(id+"F0.wireOp",EDGE,"E8.6"),sQuery(id+"F0.wireOp",EDGE,"E8.7"),sQuery(id+"F0.wireOp",EDGE,"E9.0"),sQuery(id+"F0.wireOp",EDGE,"E9.1"),sQuery(id+"F0.wireOp",EDGE,"E9.2"),sQuery(id+"F0.wireOp",EDGE,"E9.3"),sQuery(id+"F0.wireOp",EDGE,"E9.4"),sQuery(id+"F0.wireOp",EDGE,"E9.5"),sQuery(id+"F0.wireOp",EDGE,"E9.6"),sQuery(id+"F0.wireOp",EDGE,"E9.7"),subQ0,sQuery(id+"F0.wireOp",EDGE,"E11")])],"isStart":false})]});}
            var Q22;
            {var subQ0=sQuery(id+"F0.wireOp",EDGE,"E10");var subQ1=sQuery(id+"F0.wireOp",EDGE,"E8.4");Q22=makeQuery(id+"F4.opFillet","BLEND_EDGE",EDGE,{"blendedFrom":[makeQuery(id+"F2.opChamfer","BLEND_EDGE",EDGE,{"blendedFrom":[makeQuery(id+"F1.opExtrude","CAP_EDGE",EDGE,{"disambiguationData":[OSD([subQ0])],"isStart":false}),makeQuery(id+"F1.opExtrude","SWEPT_FACE",FACE,{"disambiguationData":[OSD([subQ1])]})],"blendedInto":[makeQuery(id+"F1.opExtrude","SWEPT_FACE",FACE,{"disambiguationData":[OSD([subQ1])]})]}),makeQuery(id+"F1.opExtrude","CAP_FACE",FACE,{"disambiguationData":[OSD([sQuery(id+"F0.wireOp",EDGE,"E8.0"),sQuery(id+"F0.wireOp",EDGE,"E8.1"),sQuery(id+"F0.wireOp",EDGE,"E8.2"),sQuery(id+"F0.wireOp",EDGE,"E8.3"),subQ1,sQuery(id+"F0.wireOp",EDGE,"E8.5"),sQuery(id+"F0.wireOp",EDGE,"E8.6"),sQuery(id+"F0.wireOp",EDGE,"E8.7"),sQuery(id+"F0.wireOp",EDGE,"E9.0"),sQuery(id+"F0.wireOp",EDGE,"E9.1"),sQuery(id+"F0.wireOp",EDGE,"E9.2"),sQuery(id+"F0.wireOp",EDGE,"E9.3"),sQuery(id+"F0.wireOp",EDGE,"E9.4"),sQuery(id+"F0.wireOp",EDGE,"E9.5"),sQuery(id+"F0.wireOp",EDGE,"E9.6"),sQuery(id+"F0.wireOp",EDGE,"E9.7"),subQ0,sQuery(id+"F0.wireOp",EDGE,"E11")])],"isStart":false})],"blendedInto":[makeQuery(id+"F1.opExtrude","CAP_FACE",FACE,{"disambiguationData":[OSD([sQuery(id+"F0.wireOp",EDGE,"E8.0"),sQuery(id+"F0.wireOp",EDGE,"E8.1"),sQuery(id+"F0.wireOp",EDGE,"E8.2"),sQuery(id+"F0.wireOp",EDGE,"E8.3"),subQ1,sQuery(id+"F0.wireOp",EDGE,"E8.5"),sQuery(id+"F0.wireOp",EDGE,"E8.6"),sQuery(id+"F0.wireOp",EDGE,"E8.7"),sQuery(id+"F0.wireOp",EDGE,"E9.0"),sQuery(id+"F0.wireOp",EDGE,"E9.1"),sQuery(id+"F0.wireOp",EDGE,"E9.2"),sQuery(id+"F0.wireOp",EDGE,"E9.3"),sQuery(id+"F0.wireOp",EDGE,"E9.4"),sQuery(id+"F0.wireOp",EDGE,"E9.5"),sQuery(id+"F0.wireOp",EDGE,"E9.6"),sQuery(id+"F0.wireOp",EDGE,"E9.7"),subQ0,sQuery(id+"F0.wireOp",EDGE,"E11")])],"isStart":false})]});}
            var Q23;
            Q23=makeQuery(id+"F1.opExtrude","CAP_EDGE",EDGE,{"disambiguationData":[OSD([sQuery(id+"F0.wireOp",EDGE,"E8.4")])],"isStart":false});
            var Q24;
            Q24=makeQuery(id+"F1.opExtrude","CAP_EDGE",EDGE,{"disambiguationData":[OSD([sQuery(id+"F0.wireOp",EDGE,"E8.5")])],"isStart":false});
            var Q25;
            Q25=makeQuery(id+"F1.opExtrude","CAP_EDGE",EDGE,{"disambiguationData":[OSD([sQuery(id+"F0.wireOp",EDGE,"E8.6")])],"isStart":false});
            var Q26;
            Q26=makeQuery(id+"F1.opExtrude","CAP_EDGE",EDGE,{"disambiguationData":[OSD([sQuery(id+"F0.wireOp",EDGE,"E8.7")])],"isStart":false});
            var Q27;
            Q27=makeQuery(id+"F1.opExtrude","CAP_EDGE",EDGE,{"disambiguationData":[OSD([sQuery(id+"F0.wireOp",EDGE,"E8.3")])],"isStart":false});
            var Q28;
            Q28=makeQuery(id+"F1.opExtrude","CAP_EDGE",EDGE,{"disambiguationData":[OSD([sQuery(id+"F0.wireOp",EDGE,"E8.2")])],"isStart":false});
            var Q29;
            Q29=makeQuery(id+"F1.opExtrude","CAP_EDGE",EDGE,{"disambiguationData":[OSD([sQuery(id+"F0.wireOp",EDGE,"E8.1")])],"isStart":false});
            var Q30;
            Q30=makeQuery(id+"F1.opExtrude","CAP_EDGE",EDGE,{"disambiguationData":[OSD([sQuery(id+"F0.wireOp",EDGE,"E8.0")])],"isStart":false});
            var Q31;
            {var subQ0=sQuery(id+"F0.wireOp",EDGE,"E11");var subQ1=sQuery(id+"F0.wireOp",EDGE,"E8.0");Q31=makeQuery(id+"F4.opFillet","BLEND_EDGE",EDGE,{"blendedFrom":[makeQuery(id+"F2.opChamfer","BLEND_EDGE",EDGE,{"blendedFrom":[makeQuery(id+"F1.opExtrude","CAP_EDGE",EDGE,{"disambiguationData":[OSD([subQ0])],"isStart":false}),makeQuery(id+"F1.opExtrude","SWEPT_FACE",FACE,{"disambiguationData":[OSD([subQ1])]})],"blendedInto":[makeQuery(id+"F1.opExtrude","SWEPT_FACE",FACE,{"disambiguationData":[OSD([subQ1])]})]}),makeQuery(id+"F1.opExtrude","CAP_FACE",FACE,{"disambiguationData":[OSD([subQ1,sQuery(id+"F0.wireOp",EDGE,"E8.1"),sQuery(id+"F0.wireOp",EDGE,"E8.2"),sQuery(id+"F0.wireOp",EDGE,"E8.3"),sQuery(id+"F0.wireOp",EDGE,"E8.4"),sQuery(id+"F0.wireOp",EDGE,"E8.5"),sQuery(id+"F0.wireOp",EDGE,"E8.6"),sQuery(id+"F0.wireOp",EDGE,"E8.7"),sQuery(id+"F0.wireOp",EDGE,"E9.0"),sQuery(id+"F0.wireOp",EDGE,"E9.1"),sQuery(id+"F0.wireOp",EDGE,"E9.2"),sQuery(id+"F0.wireOp",EDGE,"E9.3"),sQuery(id+"F0.wireOp",EDGE,"E9.4"),sQuery(id+"F0.wireOp",EDGE,"E9.5"),sQuery(id+"F0.wireOp",EDGE,"E9.6"),sQuery(id+"F0.wireOp",EDGE,"E9.7"),sQuery(id+"F0.wireOp",EDGE,"E10"),subQ0])],"isStart":false})],"blendedInto":[makeQuery(id+"F1.opExtrude","CAP_FACE",FACE,{"disambiguationData":[OSD([subQ1,sQuery(id+"F0.wireOp",EDGE,"E8.1"),sQuery(id+"F0.wireOp",EDGE,"E8.2"),sQuery(id+"F0.wireOp",EDGE,"E8.3"),sQuery(id+"F0.wireOp",EDGE,"E8.4"),sQuery(id+"F0.wireOp",EDGE,"E8.5"),sQuery(id+"F0.wireOp",EDGE,"E8.6"),sQuery(id+"F0.wireOp",EDGE,"E8.7"),sQuery(id+"F0.wireOp",EDGE,"E9.0"),sQuery(id+"F0.wireOp",EDGE,"E9.1"),sQuery(id+"F0.wireOp",EDGE,"E9.2"),sQuery(id+"F0.wireOp",EDGE,"E9.3"),sQuery(id+"F0.wireOp",EDGE,"E9.4"),sQuery(id+"F0.wireOp",EDGE,"E9.5"),sQuery(id+"F0.wireOp",EDGE,"E9.6"),sQuery(id+"F0.wireOp",EDGE,"E9.7"),sQuery(id+"F0.wireOp",EDGE,"E10"),subQ0])],"isStart":false})]});}
            var Q32;
            {var subQ0=sQuery(id+"F0.wireOp",EDGE,"E11");Q32=makeQuery(id+"F2.opChamfer","BLEND_EDGE",EDGE,{"blendedFrom":[makeQuery(id+"F1.opExtrude","CAP_EDGE",EDGE,{"disambiguationData":[OSD([subQ0])],"isStart":false}),makeQuery(id+"F1.opExtrude","CAP_FACE",FACE,{"disambiguationData":[OSD([sQuery(id+"F0.wireOp",EDGE,"E8.0"),sQuery(id+"F0.wireOp",EDGE,"E8.1"),sQuery(id+"F0.wireOp",EDGE,"E8.2"),sQuery(id+"F0.wireOp",EDGE,"E8.3"),sQuery(id+"F0.wireOp",EDGE,"E8.4"),sQuery(id+"F0.wireOp",EDGE,"E8.5"),sQuery(id+"F0.wireOp",EDGE,"E8.6"),sQuery(id+"F0.wireOp",EDGE,"E8.7"),sQuery(id+"F0.wireOp",EDGE,"E9.0"),sQuery(id+"F0.wireOp",EDGE,"E9.1"),sQuery(id+"F0.wireOp",EDGE,"E9.2"),sQuery(id+"F0.wireOp",EDGE,"E9.3"),sQuery(id+"F0.wireOp",EDGE,"E9.4"),sQuery(id+"F0.wireOp",EDGE,"E9.5"),sQuery(id+"F0.wireOp",EDGE,"E9.6"),sQuery(id+"F0.wireOp",EDGE,"E9.7"),sQuery(id+"F0.wireOp",EDGE,"E10"),subQ0])],"isStart":false})],"blendedInto":[makeQuery(id+"F1.opExtrude","CAP_FACE",FACE,{"disambiguationData":[OSD([sQuery(id+"F0.wireOp",EDGE,"E8.0"),sQuery(id+"F0.wireOp",EDGE,"E8.1"),sQuery(id+"F0.wireOp",EDGE,"E8.2"),sQuery(id+"F0.wireOp",EDGE,"E8.3"),sQuery(id+"F0.wireOp",EDGE,"E8.4"),sQuery(id+"F0.wireOp",EDGE,"E8.5"),sQuery(id+"F0.wireOp",EDGE,"E8.6"),sQuery(id+"F0.wireOp",EDGE,"E8.7"),sQuery(id+"F0.wireOp",EDGE,"E9.0"),sQuery(id+"F0.wireOp",EDGE,"E9.1"),sQuery(id+"F0.wireOp",EDGE,"E9.2"),sQuery(id+"F0.wireOp",EDGE,"E9.3"),sQuery(id+"F0.wireOp",EDGE,"E9.4"),sQuery(id+"F0.wireOp",EDGE,"E9.5"),sQuery(id+"F0.wireOp",EDGE,"E9.6"),sQuery(id+"F0.wireOp",EDGE,"E9.7"),sQuery(id+"F0.wireOp",EDGE,"E10"),subQ0])],"isStart":false})]});}
            var Q33;
            {var subQ0=sQuery(id+"F0.wireOp",EDGE,"E11");var subQ1=sQuery(id+"F0.wireOp",EDGE,"E9.4");Q33=makeQuery(id+"F4.opFillet","BLEND_EDGE",EDGE,{"blendedFrom":[makeQuery(id+"F2.opChamfer","BLEND_EDGE",EDGE,{"blendedFrom":[makeQuery(id+"F1.opExtrude","CAP_EDGE",EDGE,{"disambiguationData":[OSD([subQ0])],"isStart":false}),makeQuery(id+"F1.opExtrude","SWEPT_FACE",FACE,{"disambiguationData":[OSD([subQ1])]})],"blendedInto":[makeQuery(id+"F1.opExtrude","SWEPT_FACE",FACE,{"disambiguationData":[OSD([subQ1])]})]}),makeQuery(id+"F1.opExtrude","CAP_FACE",FACE,{"disambiguationData":[OSD([sQuery(id+"F0.wireOp",EDGE,"E8.0"),sQuery(id+"F0.wireOp",EDGE,"E8.1"),sQuery(id+"F0.wireOp",EDGE,"E8.2"),sQuery(id+"F0.wireOp",EDGE,"E8.3"),sQuery(id+"F0.wireOp",EDGE,"E8.4"),sQuery(id+"F0.wireOp",EDGE,"E8.5"),sQuery(id+"F0.wireOp",EDGE,"E8.6"),sQuery(id+"F0.wireOp",EDGE,"E8.7"),sQuery(id+"F0.wireOp",EDGE,"E9.0"),sQuery(id+"F0.wireOp",EDGE,"E9.1"),sQuery(id+"F0.wireOp",EDGE,"E9.2"),sQuery(id+"F0.wireOp",EDGE,"E9.3"),subQ1,sQuery(id+"F0.wireOp",EDGE,"E9.5"),sQuery(id+"F0.wireOp",EDGE,"E9.6"),sQuery(id+"F0.wireOp",EDGE,"E9.7"),sQuery(id+"F0.wireOp",EDGE,"E10"),subQ0])],"isStart":false})],"blendedInto":[makeQuery(id+"F1.opExtrude","CAP_FACE",FACE,{"disambiguationData":[OSD([sQuery(id+"F0.wireOp",EDGE,"E8.0"),sQuery(id+"F0.wireOp",EDGE,"E8.1"),sQuery(id+"F0.wireOp",EDGE,"E8.2"),sQuery(id+"F0.wireOp",EDGE,"E8.3"),sQuery(id+"F0.wireOp",EDGE,"E8.4"),sQuery(id+"F0.wireOp",EDGE,"E8.5"),sQuery(id+"F0.wireOp",EDGE,"E8.6"),sQuery(id+"F0.wireOp",EDGE,"E8.7"),sQuery(id+"F0.wireOp",EDGE,"E9.0"),sQuery(id+"F0.wireOp",EDGE,"E9.1"),sQuery(id+"F0.wireOp",EDGE,"E9.2"),sQuery(id+"F0.wireOp",EDGE,"E9.3"),subQ1,sQuery(id+"F0.wireOp",EDGE,"E9.5"),sQuery(id+"F0.wireOp",EDGE,"E9.6"),sQuery(id+"F0.wireOp",EDGE,"E9.7"),sQuery(id+"F0.wireOp",EDGE,"E10"),subQ0])],"isStart":false})]});}
            var Q34;
            Q34=makeQuery(id+"F1.opExtrude","CAP_EDGE",EDGE,{"disambiguationData":[OSD([sQuery(id+"F0.wireOp",EDGE,"E9.4")])],"isStart":false});
            var Q35;
            Q35=makeQuery(id+"F1.opExtrude","CAP_EDGE",EDGE,{"disambiguationData":[OSD([sQuery(id+"F0.wireOp",EDGE,"E9.5")])],"isStart":false});
            var Q36;
            Q36=makeQuery(id+"F1.opExtrude","CAP_EDGE",EDGE,{"disambiguationData":[OSD([sQuery(id+"F0.wireOp",EDGE,"E9.6")])],"isStart":false});
            var Q37;
            Q37=makeQuery(id+"F1.opExtrude","CAP_EDGE",EDGE,{"disambiguationData":[OSD([sQuery(id+"F0.wireOp",EDGE,"E9.7")])],"isStart":false});
            var Q38;
            Q38=makeQuery(id+"F1.opExtrude","CAP_FACE",FACE,{"disambiguationData":[OSD([sQuery(id+"F0.wireOp",EDGE,"E8.0"),sQuery(id+"F0.wireOp",EDGE,"E8.1"),sQuery(id+"F0.wireOp",EDGE,"E8.2"),sQuery(id+"F0.wireOp",EDGE,"E8.3"),sQuery(id+"F0.wireOp",EDGE,"E8.4"),sQuery(id+"F0.wireOp",EDGE,"E8.5"),sQuery(id+"F0.wireOp",EDGE,"E8.6"),sQuery(id+"F0.wireOp",EDGE,"E8.7"),sQuery(id+"F0.wireOp",EDGE,"E9.0"),sQuery(id+"F0.wireOp",EDGE,"E9.1"),sQuery(id+"F0.wireOp",EDGE,"E9.2"),sQuery(id+"F0.wireOp",EDGE,"E9.3"),sQuery(id+"F0.wireOp",EDGE,"E9.4"),sQuery(id+"F0.wireOp",EDGE,"E9.5"),sQuery(id+"F0.wireOp",EDGE,"E9.6"),sQuery(id+"F0.wireOp",EDGE,"E9.7"),sQuery(id+"F0.wireOp",EDGE,"E10"),sQuery(id+"F0.wireOp",EDGE,"E11")])],"isStart":false});
            var Q39;
            {var subQ0=sQuery(id+"F0.wireOp",EDGE,"E11");var subQ1=sQuery(id+"F0.wireOp",EDGE,"E9.4");Q39=makeQuery(id+"F4.opFillet","BLEND_EDGE",EDGE,{"blendedFrom":[makeQuery(id+"F2.opChamfer","BLEND_EDGE",EDGE,{"blendedFrom":[makeQuery(id+"F1.opExtrude","CAP_EDGE",EDGE,{"disambiguationData":[OSD([subQ0])],"isStart":true}),makeQuery(id+"F1.opExtrude","SWEPT_FACE",FACE,{"disambiguationData":[OSD([subQ1])]})],"blendedInto":[makeQuery(id+"F1.opExtrude","SWEPT_FACE",FACE,{"disambiguationData":[OSD([subQ1])]})]}),makeQuery(id+"F1.opExtrude","CAP_FACE",FACE,{"disambiguationData":[OSD([sQuery(id+"F0.wireOp",EDGE,"E8.0"),sQuery(id+"F0.wireOp",EDGE,"E8.1"),sQuery(id+"F0.wireOp",EDGE,"E8.2"),sQuery(id+"F0.wireOp",EDGE,"E8.3"),sQuery(id+"F0.wireOp",EDGE,"E8.4"),sQuery(id+"F0.wireOp",EDGE,"E8.5"),sQuery(id+"F0.wireOp",EDGE,"E8.6"),sQuery(id+"F0.wireOp",EDGE,"E8.7"),sQuery(id+"F0.wireOp",EDGE,"E9.0"),sQuery(id+"F0.wireOp",EDGE,"E9.1"),sQuery(id+"F0.wireOp",EDGE,"E9.2"),sQuery(id+"F0.wireOp",EDGE,"E9.3"),subQ1,sQuery(id+"F0.wireOp",EDGE,"E9.5"),sQuery(id+"F0.wireOp",EDGE,"E9.6"),sQuery(id+"F0.wireOp",EDGE,"E9.7"),sQuery(id+"F0.wireOp",EDGE,"E10"),subQ0])],"isStart":true})],"blendedInto":[makeQuery(id+"F1.opExtrude","CAP_FACE",FACE,{"disambiguationData":[OSD([sQuery(id+"F0.wireOp",EDGE,"E8.0"),sQuery(id+"F0.wireOp",EDGE,"E8.1"),sQuery(id+"F0.wireOp",EDGE,"E8.2"),sQuery(id+"F0.wireOp",EDGE,"E8.3"),sQuery(id+"F0.wireOp",EDGE,"E8.4"),sQuery(id+"F0.wireOp",EDGE,"E8.5"),sQuery(id+"F0.wireOp",EDGE,"E8.6"),sQuery(id+"F0.wireOp",EDGE,"E8.7"),sQuery(id+"F0.wireOp",EDGE,"E9.0"),sQuery(id+"F0.wireOp",EDGE,"E9.1"),sQuery(id+"F0.wireOp",EDGE,"E9.2"),sQuery(id+"F0.wireOp",EDGE,"E9.3"),subQ1,sQuery(id+"F0.wireOp",EDGE,"E9.5"),sQuery(id+"F0.wireOp",EDGE,"E9.6"),sQuery(id+"F0.wireOp",EDGE,"E9.7"),sQuery(id+"F0.wireOp",EDGE,"E10"),subQ0])],"isStart":true})]});}
            chamfer(context, id + "F5", {"entities" : qUnion([Q0, Q1, Q2, Q3, Q4, Q5, Q6, Q7, Q8, Q9, Q10, Q11, Q12, Q13, Q14, Q15, Q16, Q17, Q18, Q19, Q20, Q21, Q22, Q23, Q24, Q25, Q26, Q27, Q28, Q29, Q30, Q31, Q32, Q33, Q34, Q35, Q36, Q37, Q38, Q39]), "width" : 0.2 * mm, "tangentPropagation" : true});
        }
    });
